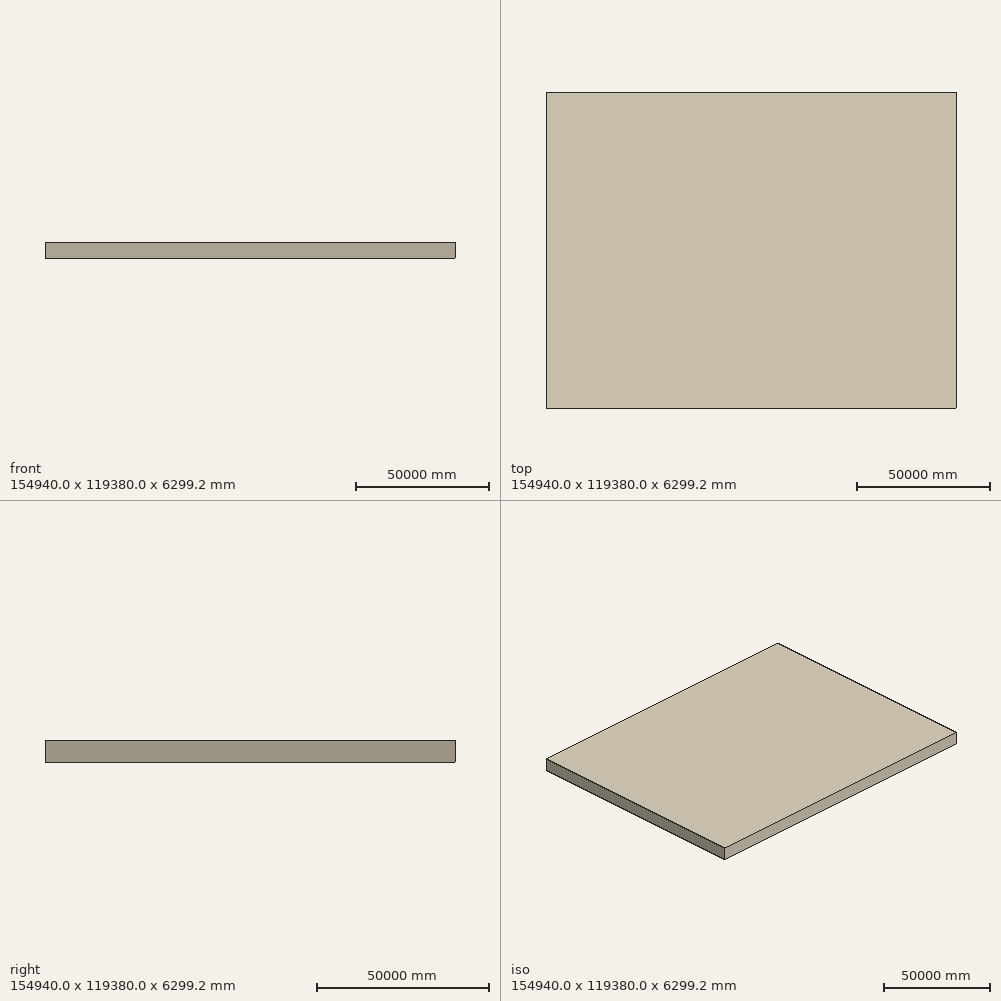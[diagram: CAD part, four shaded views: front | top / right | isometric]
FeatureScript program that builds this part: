
annotation { "Feature Type Name" : "Feature", "Feature Type Description" : "" }
export const myFeature = defineFeature(function(context is Context, id is Id, definition is map)
    precondition{}
    {
        {
            var Q0;
            Q0=qCreatedBy(makeId("Top.planeOp"),FACE);
            var sketch = newSketch(context, id + "F0", { "sketchPlane" : qUnion([Q0])});
            skLineSegment(sketch, "E0.bottom", {"start": v(0, 0) * mm, "end": v(154940, 0) * mm});
            skLineSegment(sketch, "E0.top", {"start": v(0, 119380) * mm, "end": v(154940, 119380) * mm});
            skLineSegment(sketch, "E0.left", {"start": v(0, 0) * mm, "end": v(0, 119380) * mm});
            skLineSegment(sketch, "E0.right", {"start": v(154940, 0) * mm, "end": v(154940, 119380) * mm});
            skSolve(sketch);
        }
        {
            var Q0;
            Q0=makeQuery(id+"F0.imprint","IMPRINT",FACE,{"disambiguationData":[TD([[makeQuery(id+"F0.imprint","IMPRINT",EDGE,{"derivedFrom":sQuery(id+"F0.wireOp",EDGE,"E0.bottom")}),1.0]])]});
            extrude(context, id + "F1", {"entities" : qUnion([Q0]), "depth" : 6299.2 * mm, "offsetDistance" : 25.4 * mm});
        }
    });
